# Revit family: LOROWERK 05520-150X
name_source: partatom
category: Pipe Fittings
revit_build: Autodesk Revit 2017 (Build: 20160225_1515(x64)
units: mm (PartAtom-declared; Revit-internal decimal feet)

## family parameters
Always vertical = Yes
Cut with Voids When Loaded = No
Part Type = Breaks Into
Round Connector Dimension = Use Diameter
Shared = No
Work Plane-Based = No

## types (1)
- LOROWERK 05520-150X
    Außendurchmesser Rohr [mm] = 159
    BIM = https://media.stage.bim.site
    Brandschutzklasse Text = B1 nach DIN 4102
    CONNECTOR0_DIAMETER_dZ_0r = 150 mm
    CONNECTOR0_dZ_00 = 1830 mm
    CONNECTOR0_dZ_01 = 2000 mm  [stored 6.56168 ft]
    CONNECTOR0_ref_dZ = 1830 mm
    CONNECTOR1_DIAMETER_dZ_0r = 150 mm
    CONNECTOR1_dZ_01 = 170 mm
    CONNECTOR1_ref_dZ = 170 mm
    DATANORM = 05520.150X
    Description = LORO-X Stahlabflussrohre
    GTIN = 4038088061077
    HAN = 05520.150X
    HeinzeBIM = https://www.heinze.de
    Index Number = 2
    Lieferform = Stück
    Lieferlänge [m] = 2
    Manufacturer = LOROWERK K.H. Vahlbrauk GmbH & Co. KG
    Nenndruck Text = 0.5
    Nenndrucksystem Text = PN
    Nennmaß = 150
    Nennweitensystem Text = DN
    Normen/Regeln/Zulassungen Text = DVGW für Trinkwasser
    Nutzbare Rohrlänge [m] = 2
    Produktbezeichnung Text = LORO-X Stahlabflussrohre
    Produktkennung Text = Rohr
    Produktname Text = LORO-X Regenstandrohre aus Stahl, rund, mit Reinigungsöffnung
    Produktvideo = https://media.stage.bim.site
    Querschnittsform Text = rund
    Type Name = LORO-X Regenstandrohre aus Stahl, rund, mit Reinigungsöffnung
    VDIBSN = 020001???001001???00100100000100300700000000000060000000050000200000
    Verbindungsart I Text = Pressen
    Verbindungsart II Text = axial pressen
    Verlegeart Text = Unterputz
    Wanddicke [mm] = 2.5
    Wärmeausdehnungskoeffizient Rohr [mm/(m.K)] = 0.012
    max. zul. Dauer-Betriebstemperatur [°C] Number = 95

note: [stored X ft] marks values corroborated as IEEE doubles in the binary element streams (Revit-internal decimal feet)

## geometry (parser evidence)
native form markers: Blend x2
no freeform markers — native parametric forms only
